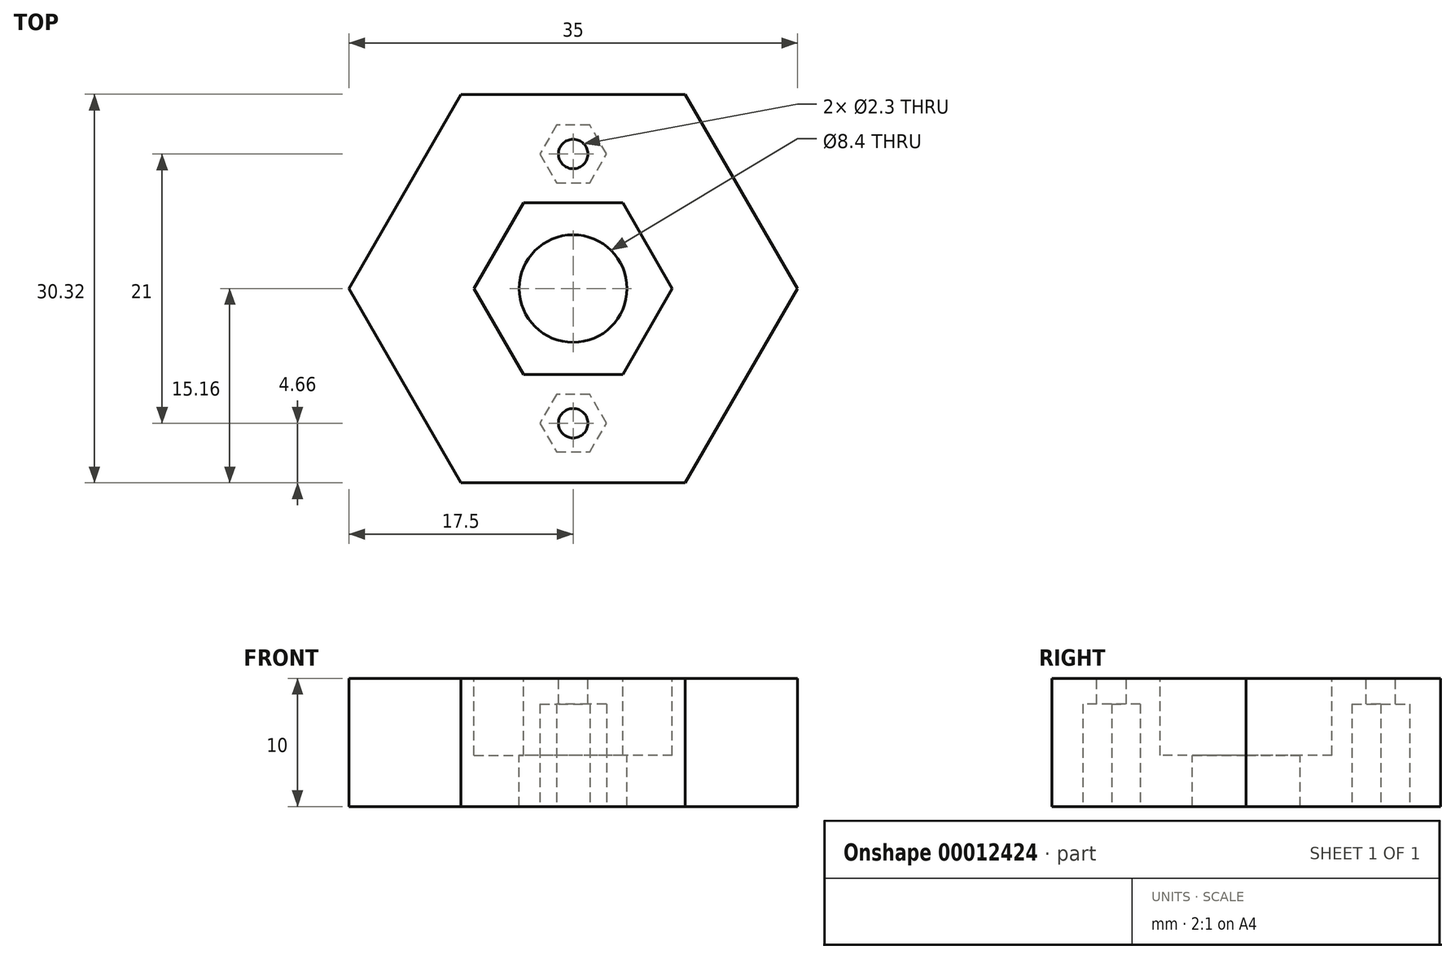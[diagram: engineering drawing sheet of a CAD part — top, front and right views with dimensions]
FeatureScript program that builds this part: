
annotation { "Feature Type Name" : "Feature", "Feature Type Description" : "" }
export const myFeature = defineFeature(function(context is Context, id is Id, definition is map)
    precondition{}
    {
        {
            var Q0;
            Q0=qCreatedBy(makeId("Top.planeOp"),FACE);
            var sketch = newSketch(context, id + "F0", { "sketchPlane" : qUnion([Q0])});
            skCircle(sketch, "E0.cCircle", {"center": v(0, 0) * mm, "radius": 17.5 * mm, "construction": true});
            skLineSegment(sketch, "E0.0", {"start": v(8.75, 15.16) * mm, "end": v(17.5, 0) * mm});
            skLineSegment(sketch, "E0.1", {"start": v(17.5, 0) * mm, "end": v(8.75, -15.16) * mm});
            skLineSegment(sketch, "E0.2", {"start": v(8.75, -15.16) * mm, "end": v(-8.75, -15.16) * mm});
            skLineSegment(sketch, "E0.3", {"start": v(-8.75, -15.16) * mm, "end": v(-17.5, 0) * mm});
            skLineSegment(sketch, "E0.4", {"start": v(-17.5, 0) * mm, "end": v(-8.75, 15.16) * mm});
            skLineSegment(sketch, "E0.5", {"start": v(-8.75, 15.16) * mm, "end": v(8.75, 15.16) * mm});
            skSolve(sketch);
        }
        {
            var Q0;
            Q0 = qSketchRegion(id + "F0", true);
            extrude(context, id + "F1", {"entities" : qUnion([Q0]), "depth" : 10 * mm});
        }
        {
            var Q0;
            Q0=makeQuery(id+"F1.opExtrude","CAP_FACE",FACE,{"disambiguationData":[OSD([sQuery(id+"F0.wireOp",EDGE,"E0.0"),sQuery(id+"F0.wireOp",EDGE,"E0.1"),sQuery(id+"F0.wireOp",EDGE,"E0.2"),sQuery(id+"F0.wireOp",EDGE,"E0.3"),sQuery(id+"F0.wireOp",EDGE,"E0.4"),sQuery(id+"F0.wireOp",EDGE,"E0.5")])],"isStart":false});
            var sketch = newSketch(context, id + "F2", { "sketchPlane" : qUnion([Q0])});
            skCircle(sketch, "E1", {"center": v(0, 0) * mm, "radius": 4.2 * mm});
            skSolve(sketch);
        }
        {
            var Q0;
            Q0 = qSketchRegion(id + "F2", true);
            extrude(context, id + "F3", {"entities" : qUnion([Q0]), "operationType" : NewBodyOperationType.REMOVE, "endBound" : BoundingType.THROUGH_ALL, "oppositeDirection" : true, "depth" : 25 * mm});
        }
        {
            var Q0;
            Q0=makeQuery(id+"F1.opExtrude","CAP_FACE",FACE,{"disambiguationData":[OSD([sQuery(id+"F0.wireOp",EDGE,"E0.0"),sQuery(id+"F0.wireOp",EDGE,"E0.1"),sQuery(id+"F0.wireOp",EDGE,"E0.2"),sQuery(id+"F0.wireOp",EDGE,"E0.3"),sQuery(id+"F0.wireOp",EDGE,"E0.4"),sQuery(id+"F0.wireOp",EDGE,"E0.5")])],"isStart":false});
            var sketch = newSketch(context, id + "F4", { "sketchPlane" : qUnion([Q0])});
            skCircle(sketch, "E2.cCircle", {"center": v(0, 0) * mm, "radius": 6.7 * mm, "construction": true});
            skLineSegment(sketch, "E2.0", {"start": v(3.87, -6.7) * mm, "end": v(-3.87, -6.7) * mm});
            skLineSegment(sketch, "E2.1", {"start": v(-3.87, -6.7) * mm, "end": v(-7.74, 0) * mm});
            skLineSegment(sketch, "E2.2", {"start": v(-7.74, 0) * mm, "end": v(-3.87, 6.7) * mm});
            skLineSegment(sketch, "E2.3", {"start": v(-3.87, 6.7) * mm, "end": v(3.87, 6.7) * mm});
            skLineSegment(sketch, "E2.4", {"start": v(3.87, 6.7) * mm, "end": v(7.74, 0) * mm});
            skLineSegment(sketch, "E2.5", {"start": v(7.74, 0) * mm, "end": v(3.87, -6.7) * mm});
            skPoint(sketch, "E2.0.midPoint", {"position": v(0, -6.7) * mm});
            skSolve(sketch);
        }
        {
            var Q0;
            Q0 = qSketchRegion(id + "F4", true);
            extrude(context, id + "F5", {"entities" : qUnion([Q0]), "operationType" : NewBodyOperationType.REMOVE, "oppositeDirection" : true, "depth" : 6 * mm});
        }
        {
            var Q0;
            Q0=makeQuery(id+"F1.opExtrude","CAP_FACE",FACE,{"disambiguationData":[OSD([sQuery(id+"F0.wireOp",EDGE,"E0.0"),sQuery(id+"F0.wireOp",EDGE,"E0.1"),sQuery(id+"F0.wireOp",EDGE,"E0.2"),sQuery(id+"F0.wireOp",EDGE,"E0.3"),sQuery(id+"F0.wireOp",EDGE,"E0.4"),sQuery(id+"F0.wireOp",EDGE,"E0.5")])],"isStart":false});
            var sketch = newSketch(context, id + "F6", { "sketchPlane" : qUnion([Q0])});
            skLineSegment(sketch, "E3", {"start": v(0, -10.5) * mm, "end": v(0, 10.5) * mm, "construction": true});
            skPoint(sketch, "E4", {"position": v(0, 0) * mm});
            skCircle(sketch, "E5", {"center": v(0, 10.5) * mm, "radius": 1.15 * mm});
            skCircle(sketch, "E6", {"center": v(0, -10.5) * mm, "radius": 1.15 * mm});
            skSolve(sketch);
        }
        {
            var Q0;
            Q0 = qSketchRegion(id + "F6", true);
            extrude(context, id + "F7", {"entities" : qUnion([Q0]), "operationType" : NewBodyOperationType.REMOVE, "endBound" : BoundingType.THROUGH_ALL, "oppositeDirection" : true, "depth" : 25 * mm});
        }
        {
            var Q0;
            Q0=makeQuery(id+"F1.opExtrude","CAP_FACE",FACE,{"disambiguationData":[OSD([sQuery(id+"F0.wireOp",EDGE,"E0.0"),sQuery(id+"F0.wireOp",EDGE,"E0.1"),sQuery(id+"F0.wireOp",EDGE,"E0.2"),sQuery(id+"F0.wireOp",EDGE,"E0.3"),sQuery(id+"F0.wireOp",EDGE,"E0.4"),sQuery(id+"F0.wireOp",EDGE,"E0.5")])],"isStart":true});
            var sketch = newSketch(context, id + "F8", { "sketchPlane" : qUnion([Q0])});
            skCircle(sketch, "E7.cCircle", {"center": v(0, -10.5) * mm, "radius": 2.25 * mm, "construction": true});
            skLineSegment(sketch, "E7.0", {"start": v(1.3, -12.75) * mm, "end": v(-1.3, -12.75) * mm});
            skLineSegment(sketch, "E7.1", {"start": v(-1.3, -12.75) * mm, "end": v(-2.6, -10.5) * mm});
            skLineSegment(sketch, "E7.2", {"start": v(-2.6, -10.5) * mm, "end": v(-1.3, -8.25) * mm});
            skLineSegment(sketch, "E7.3", {"start": v(-1.3, -8.25) * mm, "end": v(1.3, -8.25) * mm});
            skLineSegment(sketch, "E7.4", {"start": v(1.3, -8.25) * mm, "end": v(2.6, -10.5) * mm});
            skLineSegment(sketch, "E7.5", {"start": v(2.6, -10.5) * mm, "end": v(1.3, -12.75) * mm});
            skPoint(sketch, "E7.0.midPoint", {"position": v(0, -12.75) * mm});
            skCircle(sketch, "E8.cCircle", {"center": v(0, 10.5) * mm, "radius": 2.25 * mm, "construction": true});
            skLineSegment(sketch, "E8.0", {"start": v(-1.3, 12.75) * mm, "end": v(1.3, 12.75) * mm});
            skLineSegment(sketch, "E8.1", {"start": v(1.3, 12.75) * mm, "end": v(2.6, 10.5) * mm});
            skLineSegment(sketch, "E8.2", {"start": v(2.6, 10.5) * mm, "end": v(1.3, 8.25) * mm});
            skLineSegment(sketch, "E8.3", {"start": v(1.3, 8.25) * mm, "end": v(-1.3, 8.25) * mm});
            skLineSegment(sketch, "E8.4", {"start": v(-1.3, 8.25) * mm, "end": v(-2.6, 10.5) * mm});
            skLineSegment(sketch, "E8.5", {"start": v(-2.6, 10.5) * mm, "end": v(-1.3, 12.75) * mm});
            skPoint(sketch, "E8.0.midPoint", {"position": v(0, 12.75) * mm});
            skSolve(sketch);
        }
        {
            var Q0;
            Q0 = qSketchRegion(id + "F8", true);
            extrude(context, id + "F9", {"entities" : qUnion([Q0]), "operationType" : NewBodyOperationType.REMOVE, "oppositeDirection" : true, "depth" : 8 * mm});
        }
    });
